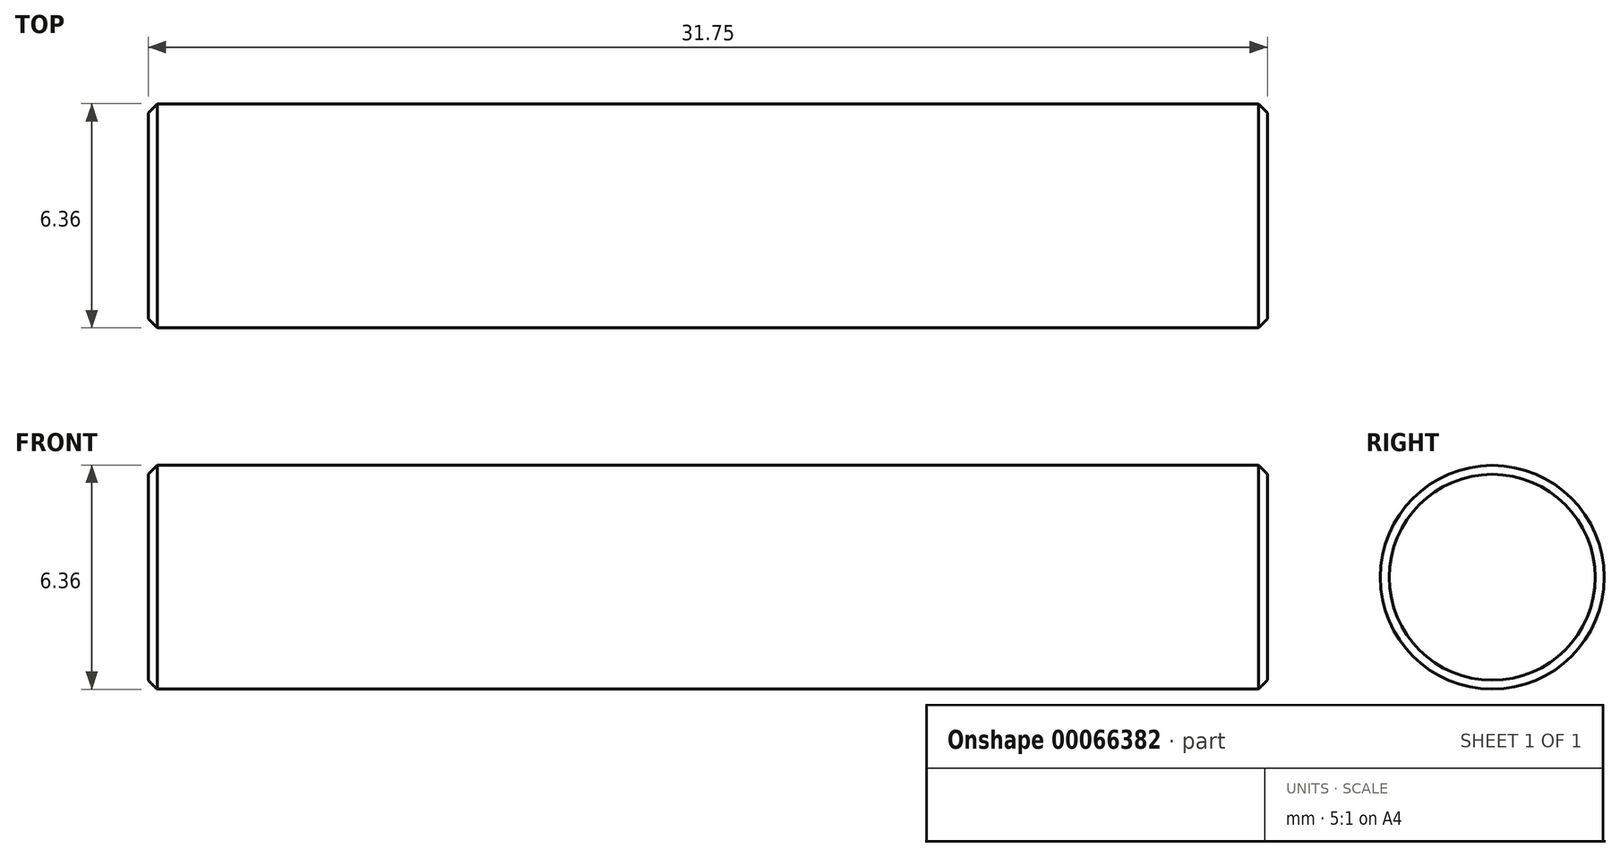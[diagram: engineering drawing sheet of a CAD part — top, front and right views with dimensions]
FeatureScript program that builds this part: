
annotation { "Feature Type Name" : "Feature", "Feature Type Description" : "" }
export const myFeature = defineFeature(function(context is Context, id is Id, definition is map)
    precondition{}
    {
        {
            var Q0;
            Q0=qCreatedBy(makeId("Right.planeOp"),FACE);
            var sketch = newSketch(context, id + "F0", { "sketchPlane" : qUnion([Q0])});
            skCircle(sketch, "E0", {"center": v(0, 0) * mm, "radius": 3.18 * mm});
            skSolve(sketch);
        }
        {
            var Q0;
            Q0 = qSketchRegion(id + "F0", true);
            extrude(context, id + "F1", {"entities" : qUnion([Q0]), "depth" : 31.75 * mm});
        }
        {
            var Q0;
            Q0=makeQuery(id+"F1.opExtrude","CAP_EDGE",EDGE,{"disambiguationData":[OSD([sQuery(id+"F0.wireOp",EDGE,"E0")])],"isStart":false});
            var Q1;
            Q1=makeQuery(id+"F1.opExtrude","CAP_EDGE",EDGE,{"disambiguationData":[OSD([sQuery(id+"F0.wireOp",EDGE,"E0")])],"isStart":true});
            chamfer(context, id + "F2", {"entities" : qUnion([Q0, Q1]), "width" : 0.25 * mm, "tangentPropagation" : true});
        }
    });
